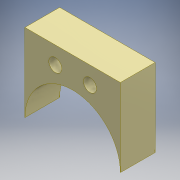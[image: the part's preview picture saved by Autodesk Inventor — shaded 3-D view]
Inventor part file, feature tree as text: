
AUTODESK INVENTOR PART (.ipt)
format: ipt  version: 2016 (Build 200138000, 138)  size: 100,352 bytes
history: native  units: mm
features: other x1, extrude x1, sketch x1
ambient origin geometry x8: Origin, YZ Plane, XZ Plane, XY Plane, X Axis, Y Axis, Z Axis, Center Point
bodies: Body1 (feature_tree)
feature tree (3):
  other  "Sólido1"
  extrude  "Extrusión1"  Depth=8.0mm TaperAngle=0.0deg
  sketch  "Boceto1"  dims[d0=3.0mm d1=4.0mm d2=7.0mm d3=3.0mm d4=7.0mm d5=4.0mm d6=8.0mm d7=0.0mm]
